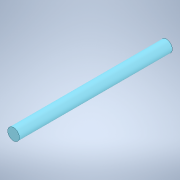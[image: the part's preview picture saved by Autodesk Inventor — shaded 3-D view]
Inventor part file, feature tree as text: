
AUTODESK INVENTOR PART (.ipt)
format: ipt  version: 2022 (Build 260153000, 153)  size: 99,840 bytes
history: native  units: in
note: dims shown in document units (in); Inventor stores cm internally (conversion verified against a paired STEP export)
features: extrude x1, sketch x1
ambient origin geometry x8: Origin, YZ Plane, XZ Plane, XY Plane, X Axis, Y Axis, Z Axis, Center Point
bodies: Solid1 (feature_tree)
feature tree (2):
  extrude  "Extrusion1"  [1 undecoded]
  sketch  "Sketch2"  dims[d0=3.937in d1=0.0in]
note: 1 required parameter value undecoded (feature->parameter linkage not recoverable at this tier; creation-order binding heuristic only, values carry confidence <= 0.55)
